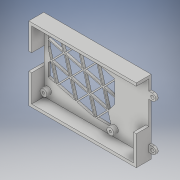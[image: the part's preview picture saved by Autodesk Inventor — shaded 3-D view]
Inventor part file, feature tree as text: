
AUTODESK INVENTOR PART (.ipt)
format: ipt  version: 2019 (Build 230136000, 136)  size: 350,208 bytes
history: native  units: in
note: dims shown in document units (in); Inventor stores cm internally (conversion verified against a paired STEP export)
features: extrude x5, sketch x2
ambient origin geometry x8: Origin, YZ Plane, XZ Plane, XY Plane, X Axis, Y Axis, Z Axis, Center Point
bodies: Solid1 (feature_tree)
feature tree (7):
  sketch  "Sketch1"  dims[d0=0.0787in d1=0.0787in]
  extrude  "Extrusion1"  Depth=0.0787in
  extrude  "Extrusion2"  Depth=0.0787in
  extrude  "Extrusion3"  Depth=0.0787in
  extrude  "Extrusion4"  Depth=1.9291in
  extrude  "Extrusion5"  Depth=0.2362in
  sketch  "Sketch2"  dims[d2=2.2835in d3=0.0787in d4=0.0787in d5=1.9291in d6=0.2362in d7=0.2362in d8=0.2362in d9=0.2362in d10=0.126in d11=0.0984in d12=0.126in d14=0.5906in d17=0.2559in d18=0.0984in d19=1.1614in d20=0.126in d21=0.0984in d22=0.6496in d23=0.1181in d24=0.1181in d25=0.2362in d26=0.1181in d27=0.1181in d28=0.2362in d29=0.3543in d30=0.1181in d31=0.2362in d32=0.1181in d33=0.1181in d34=0.2362in d35=0.0984in d36=0.1181in d37=0.0787in d38=0.0in d39=0.2362in d40=0.0in d41=0.0984in d42=0.0984in d43=0.5118in d44=0.0in d45=0.5118in d46=0.0in d62=0.5906in d63=0.5906in d64=0.5906in d66=0.5906in d67=0.5906in d68=0.5906in d69=0.0866in d73=0.0866in d75=0.5906in d76=0.0433in d77=0.5906in d78=0.0433in d79=0.5906in d81=0.5906in d82=0.5906in d83=0.5906in d84=0.0433in d85=0.0375in d86=60.0deg d87=0.0375in d88=0.5906in d90=60.0deg d91=60.0deg d92=60.0deg d93=0.0433in d94=60.0deg d95=60.0deg d96=0.0433in d97=60.0deg d98=0.5118in d99=0.0in]
